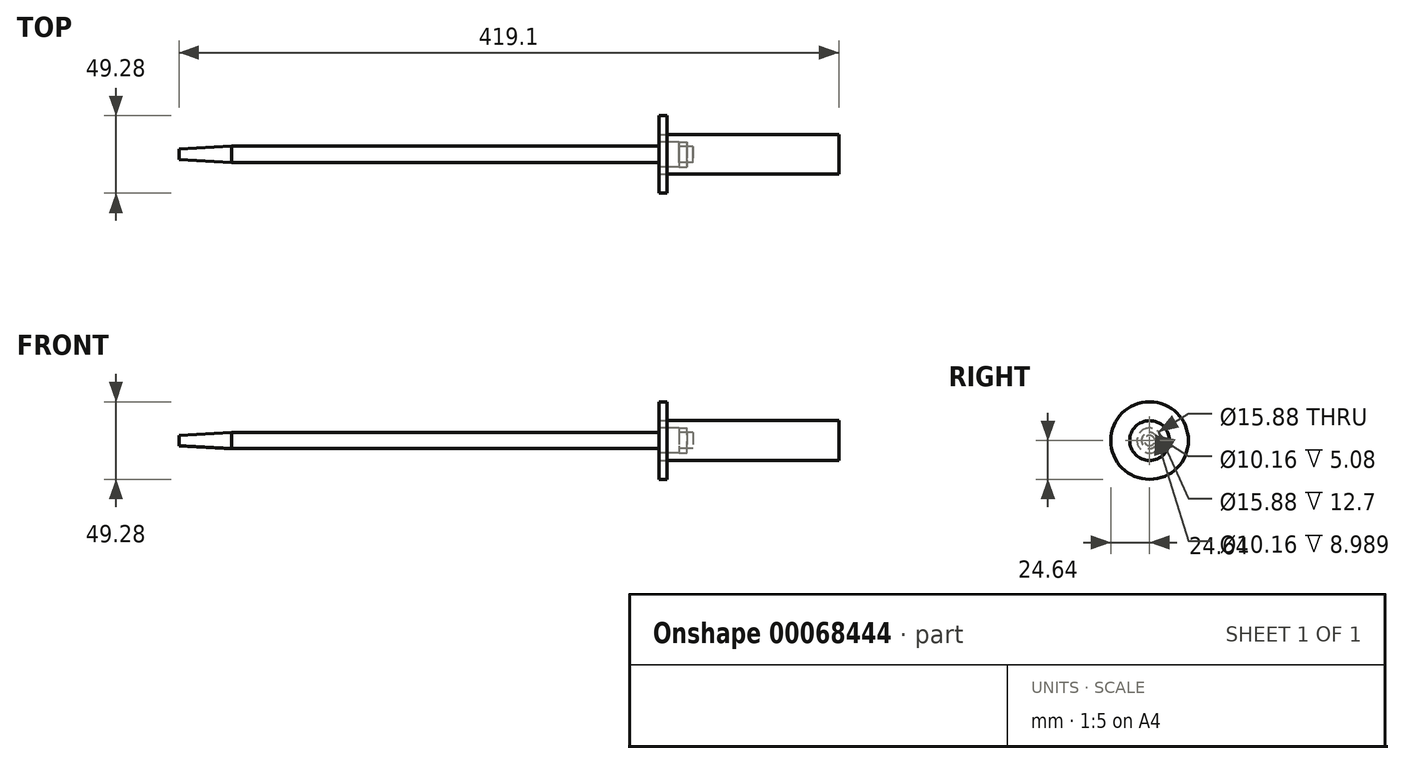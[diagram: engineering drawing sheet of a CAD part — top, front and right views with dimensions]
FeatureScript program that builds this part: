
annotation { "Feature Type Name" : "Feature", "Feature Type Description" : "" }
export const myFeature = defineFeature(function(context is Context, id is Id, definition is map)
    precondition{}
    {
        {
            var Q0;
            Q0=qCreatedBy(makeId("Front.planeOp"),FACE);
            var sketch = newSketch(context, id + "F0", { "sketchPlane" : qUnion([Q0])});
            skLineSegment(sketch, "E0", {"start": v(0, 0) * mm, "end": v(0, 12.64) * mm});
            skLineSegment(sketch, "E1", {"start": v(0, 12.64) * mm, "end": v(114.3, 12.64) * mm});
            skLineSegment(sketch, "E2", {"start": v(114.3, 12.64) * mm, "end": v(114.3, 0) * mm});
            skLineSegment(sketch, "E3", {"start": v(114.3, 0) * mm, "end": v(0, 0) * mm});
            skSolve(sketch);
        }
        {
            var Q0;
            Q0=makeQuery(id+"F0.imprint","IMPRINT",FACE,{"disambiguationData":[TD([[makeQuery(id+"F0.imprint","IMPRINT",EDGE,{"derivedFrom":sQuery(id+"F0.wireOp",EDGE,"E0")}),-1.0]])]});
            var Q1;
            Q1=sQuery(id+"F0.wireOp",EDGE,"E3");
            revolve(context, id + "F1", {"entities" : qUnion([Q0]), "axis" : qUnion([Q1]), "revolveType" : RevolveType.FULL});
        }
        {
            var Q0;
            Q0=qCreatedBy(makeId("Front.planeOp"),FACE);
            var sketch = newSketch(context, id + "F2", { "sketchPlane" : qUnion([Q0])});
            skLineSegment(sketch, "E4", {"start": v(0, 0) * mm, "end": v(0, 24.64) * mm});
            skLineSegment(sketch, "E5", {"start": v(0, 24.64) * mm, "end": v(5.08, 24.64) * mm});
            skLineSegment(sketch, "E6", {"start": v(5.08, 24.64) * mm, "end": v(5.08, 7.94) * mm});
            skLineSegment(sketch, "E7", {"start": v(5.08, 7.94) * mm, "end": v(17.78, 7.94) * mm});
            skLineSegment(sketch, "E8", {"start": v(17.78, 7.94) * mm, "end": v(17.78, 0) * mm});
            skLineSegment(sketch, "E9", {"start": v(17.78, 0) * mm, "end": v(0, 0) * mm});
            skSolve(sketch);
        }
        {
            var Q0;
            Q0=makeQuery(id+"F2.imprint","IMPRINT",FACE,{"disambiguationData":[TD([[makeQuery(id+"F2.imprint","IMPRINT",EDGE,{"derivedFrom":sQuery(id+"F2.wireOp",EDGE,"E4")}),-1.0]])]});
            var Q1;
            Q1 = qSketchRegion(id + "F4", true);
            var Q2;
            Q2=sQuery(id+"F2.wireOp",EDGE,"E9");
            revolve(context, id + "F3", {"entities" : qUnion([Q0, Q1]), "axis" : qUnion([Q2]), "revolveType" : RevolveType.FULL});
        }
        {
            var Q0;
            Q0=makeQuery(id+"F3.opRevolve","SWEPT_FACE",FACE,{"disambiguationData":[OSD([sQuery(id+"F2.wireOp",EDGE,"E4")])]});
            var sketch = newSketch(context, id + "F4", { "sketchPlane" : qUnion([Q0])});
            skCircle(sketch, "E10", {"center": v(0, 0) * mm, "radius": 5.08 * mm});
            skSolve(sketch);
        }
        {
            var Q0;
            Q0 = qSketchRegion(id + "F4", true);
            extrude(context, id + "F5", {"entities" : qUnion([Q0]), "operationType" : NewBodyOperationType.REMOVE, "oppositeDirection" : true, "depth" : 21.7 * mm});
        }
        {
            var Q0;
            Q0=makeQuery(id+"F1.opRevolve","SWEPT_FACE",FACE,{"disambiguationData":[OSD([sQuery(id+"F0.wireOp",EDGE,"E0")])]});
            var sketch = newSketch(context, id + "F6", { "sketchPlane" : qUnion([Q0])});
            skCircle(sketch, "E11", {"center": v(0, 0) * mm, "radius": 7.94 * mm});
            skSolve(sketch);
        }
        {
            var Q0;
            Q0=makeQuery(id+"F6.imprint","IMPRINT",FACE,{"disambiguationData":[TD([[makeQuery(id+"F6.imprint","IMPRINT",EDGE,{"derivedFrom":sQuery(id+"F6.wireOp",EDGE,"E11")}),1.0]])]});
            extrude(context, id + "F7", {"entities" : qUnion([Q0]), "operationType" : NewBodyOperationType.REMOVE, "oppositeDirection" : true, "depth" : 12.7 * mm});
        }
        {
            var Q0;
            Q0=qCreatedBy(makeId("Front.planeOp"),FACE);
            var sketch = newSketch(context, id + "F8", { "sketchPlane" : qUnion([Q0])});
            skLineSegment(sketch, "E12", {"start": v(0, 0) * mm, "end": v(-304.8, 0) * mm});
            skLineSegment(sketch, "E13", {"start": v(-304.8, 0) * mm, "end": v(-304.8, 3.3) * mm});
            skLineSegment(sketch, "E14", {"start": v(-304.8, 3.3) * mm, "end": v(-271.27, 5.13) * mm});
            skLineSegment(sketch, "E15", {"start": v(-271.27, 5.13) * mm, "end": v(0, 5.13) * mm});
            skLineSegment(sketch, "E16", {"start": v(0, 5.13) * mm, "end": v(0, 0) * mm});
            skLineSegment(sketch, "E17", {"start": v(-246.15, 5.13) * mm, "end": v(-341, 5.13) * mm, "construction": true});
            skSolve(sketch);
        }
        {
            var Q0;
            Q0=makeQuery(id+"F8.imprint","IMPRINT",FACE,{"disambiguationData":[TD([[makeQuery(id+"F8.imprint","IMPRINT",EDGE,{"derivedFrom":sQuery(id+"F8.wireOp",EDGE,"E12")}),-1.0]])]});
            var Q1;
            Q1=sQuery(id+"F8.wireOp",EDGE,"E12");
            var Q2;
            Q2=sQuery(id+"F8.wireOp",EDGE,"E14");
            var Q3;
            Q3=sQuery(id+"F8.wireOp",EDGE,"E15");
            var Q4;
            Q4=sQuery(id+"F8.wireOp",EDGE,"E13");
            var Q5;
            Q5=sQuery(id+"F8.wireOp",EDGE,"E16");
            var Q6;
            Q6=sQuery(id+"F8.wireOp",EDGE,"E12");
            revolve(context, id + "F9", {"entities" : qUnion([Q0]), "surfaceEntities" : qUnion([Q1, Q2, Q3, Q4, Q5]), "axis" : qUnion([Q6]), "revolveType" : RevolveType.FULL});
        }
    });
